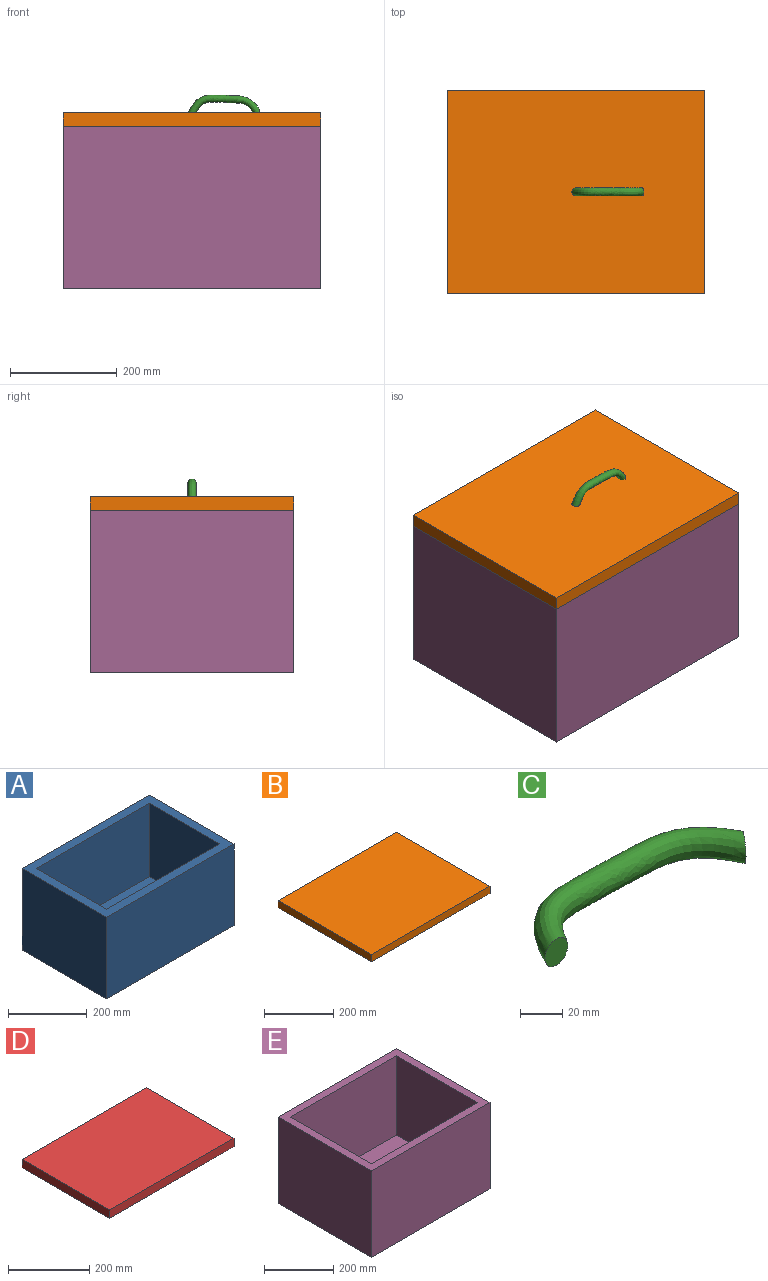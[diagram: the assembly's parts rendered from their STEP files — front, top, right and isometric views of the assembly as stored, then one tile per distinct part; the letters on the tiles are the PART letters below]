
ASSEMBLY  parts=5 mates=4
PART A: 11 faces, bbox 457.2x304.8x254 mm
  f0: plane 457.2x304.8mm, normal (0,0,1), area 36129mm2, adj f1,f2,f3,f4,f6,f7,f8,f9
  f1: plane 304.8x254mm, normal (-1,0,0), area 77419.2mm2, adj f0,f2,f4,f5
  f2: plane 457.2x254mm, normal (0,-1,0), area 116128.8mm2, adj f0,f1,f3,f5
  f3: plane 304.8x254mm, normal (1,0,0), area 77419.2mm2, adj f0,f2,f4,f5
  f4: plane 457.2x254mm, normal (0,1,0), area 116128.8mm2, adj f0,f1,f3,f5
  f5: plane 457.2x304.8mm, normal (0,0,-1), area 139354.6mm2, adj f1,f2,f3,f4
  f6: plane 254x228.6mm, normal (1,0,0), area 58064.4mm2, adj f0,f7,f9,f10
  f7: plane 406.4x228.6mm, normal (0,1,0), area 92903mm2, adj f0,f6,f8,f10
  f8: plane 254x228.6mm, normal (-1,0,0), area 58064.4mm2, adj f0,f7,f9,f10
  f9: plane 406.4x228.6mm, normal (0,-1,0), area 92903mm2, adj f0,f6,f8,f10
  f10: plane 406.4x254mm, normal (0,0,1), area 103225.6mm2, adj f6,f7,f8,f9
PART B: 6 faces, bbox 482.6x381x25.4 mm
  f0: plane 381x25.4mm, normal (-1,0,0), area 9677.4mm2, adj f1,f3,f4,f5
  f1: plane 482.6x25.4mm, normal (0,-1,0), area 12258mm2, adj f0,f2,f4,f5
  f2: plane 381x25.4mm, normal (1,0,0), area 9677.4mm2, adj f1,f3,f4,f5
  f3: plane 482.6x25.4mm, normal (0,1,0), area 12258mm2, adj f0,f2,f4,f5
  f4: plane 482.6x381mm, normal (0,0,1), area 183870.6mm2, adj f0,f1,f2,f3
  f5: plane 482.6x381mm, normal (0,0,-1), area 183870.6mm2, adj f0,f1,f2,f3
PART C: 3 faces, bbox 147.3x54.4x15.2 mm
  f0: plane 15.24x15.24mm, normal (0,-1,0), area 182.4mm2, adj f2
  f1: plane 15.24x12.12mm, normal (0.8,-0.61,0), area 182.4mm2, adj f2
  f2: bspline ~147.28x54.35mm, area 6619.3mm2, adj f0,f1
PART D: 6 faces, bbox 431.8x304.8x25.4 mm
  f0: plane 304.8x25.4mm, normal (-1,0,0), area 7741.9mm2, adj f1,f3,f4,f5
  f1: plane 431.8x25.4mm, normal (0,-1,0), area 10967.7mm2, adj f0,f2,f4,f5
  f2: plane 304.8x25.4mm, normal (1,0,0), area 7741.9mm2, adj f1,f3,f4,f5
  f3: plane 431.8x25.4mm, normal (0,1,0), area 10967.7mm2, adj f0,f2,f4,f5
  f4: plane 431.8x304.8mm, normal (0,0,1), area 131612.6mm2, adj f0,f1,f2,f3
  f5: plane 431.8x304.8mm, normal (0,0,-1), area 131612.6mm2, adj f0,f1,f2,f3
PART E: 11 faces, bbox 482.6x381x304.8 mm
  f0: plane 482.6x381mm, normal (0,0,1), area 41290.2mm2, adj f1,f2,f3,f4,f6,f7,f8,f9
  f1: plane 381x304.8mm, normal (-1,0,0), area 116128.8mm2, adj f0,f2,f4,f5
  f2: plane 482.6x304.8mm, normal (0,-1,0), area 147096.5mm2, adj f0,f1,f3,f5
  f3: plane 381x304.8mm, normal (1,0,0), area 116128.8mm2, adj f0,f2,f4,f5
  f4: plane 482.6x304.8mm, normal (0,1,0), area 147096.5mm2, adj f0,f1,f3,f5
  f5: plane 482.6x381mm, normal (0,0,-1), area 183870.6mm2, adj f1,f2,f3,f4
  f6: plane 330.2x279.4mm, normal (1,0,0), area 92257.9mm2, adj f0,f7,f9,f10
  f7: plane 431.8x279.4mm, normal (0,1,0), area 120644.9mm2, adj f0,f6,f8,f10
  f8: plane 330.2x279.4mm, normal (-1,0,0), area 92257.9mm2, adj f0,f7,f9,f10
  f9: plane 431.8x279.4mm, normal (0,-1,0), area 120644.9mm2, adj f0,f6,f8,f10
  f10: plane 431.8x330.2mm, normal (0,0,1), area 142580.4mm2, adj f6,f7,f8,f9
PLACE A t=(0,0,485.14)mm
PLACE B t=(0,0,764.54)mm
PLACE C rot(axis=(1,0,0),90deg) t=(53.91,0,789.94)mm
PLACE D t=(0,0,741.68)mm
PLACE E t=(0,0,459.74)mm
MATE planar C.f0 <-> B.f4  axis (0,0,-1) through (0,0,789.94)mm
MATE planar E.f10 <-> A.f5  axis (0,0,1) through (0,0,485.14)mm
MATE parallel B.f4 <-> E.f0  axis (0,0,1) through (0,0,789.94)mm
MATE planar B.f5 <-> E.f0  axis (0,0,-1) through (0,0,764.54)mm
